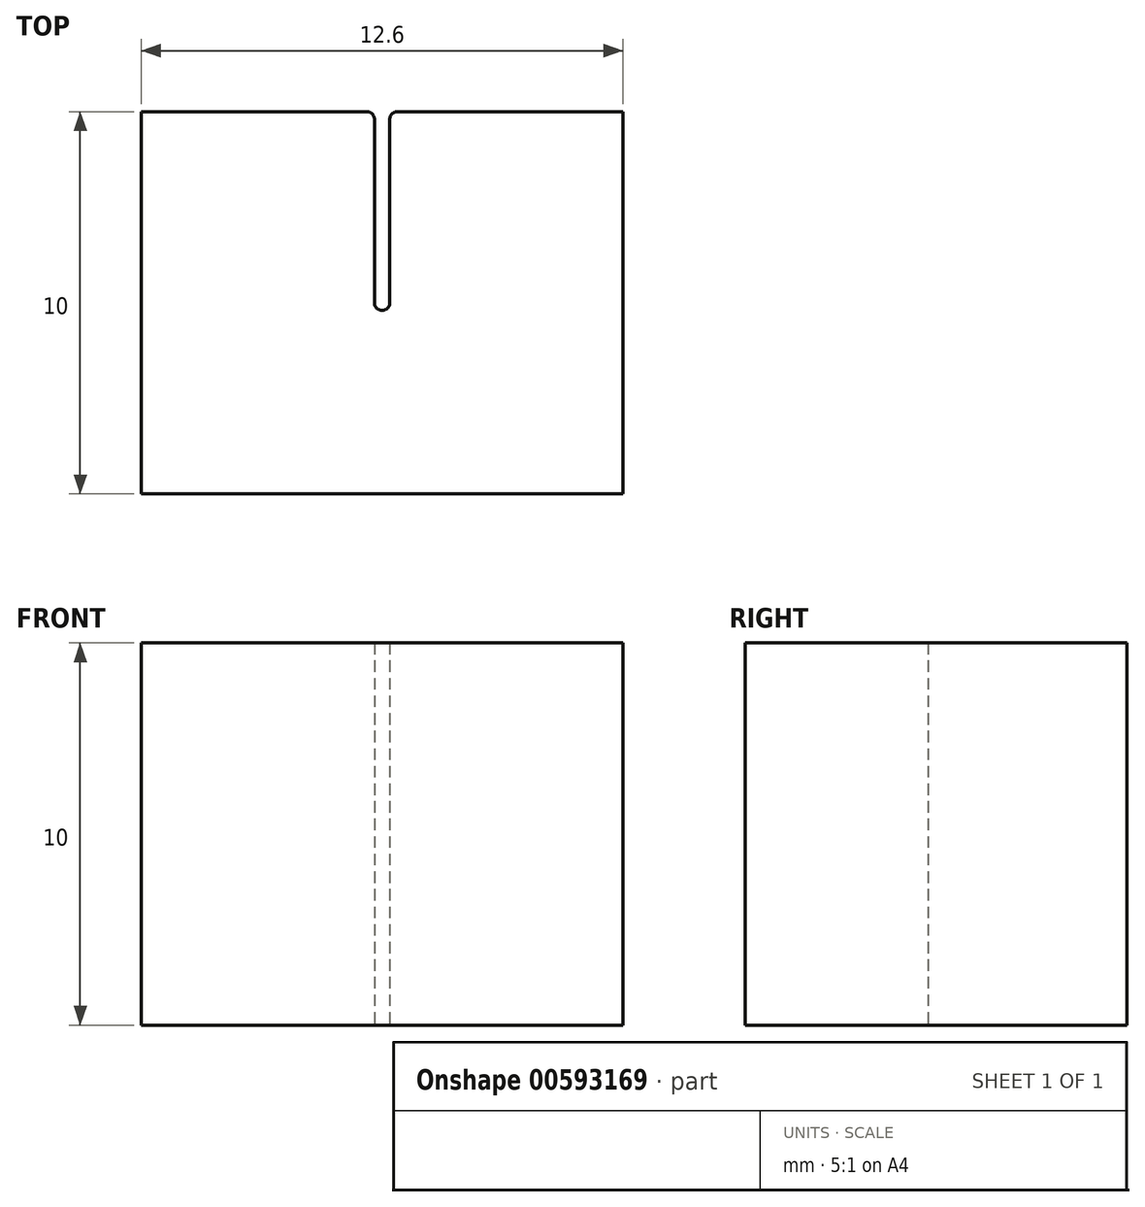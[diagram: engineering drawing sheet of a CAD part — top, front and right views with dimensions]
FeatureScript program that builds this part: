
annotation { "Feature Type Name" : "Feature", "Feature Type Description" : "" }
export const myFeature = defineFeature(function(context is Context, id is Id, definition is map)
    precondition{}
    {
        {
            var Q0;
            Q0=qCreatedBy(makeId("Top.planeOp"),FACE);
            var sketch = newSketch(context, id + "F0", { "sketchPlane" : qUnion([Q0])});
            skLineSegment(sketch, "E0.bottom", {"start": v(-6.3, 5) * mm, "end": v(-0.4, 5) * mm});
            skLineSegment(sketch, "E0.top", {"start": v(-6.3, -5) * mm, "end": v(6.3, -5) * mm});
            skLineSegment(sketch, "E0.left", {"start": v(-6.3, 5) * mm, "end": v(-6.3, -5) * mm});
            skLineSegment(sketch, "E0.right", {"start": v(6.3, 5) * mm, "end": v(6.3, -5) * mm});
            skLineSegment(sketch, "E1.top", {"start": v(0, -0.2) * mm, "end": v(0, -0.2) * mm});
            skLineSegment(sketch, "E1.left", {"start": v(-0.2, 4.8) * mm, "end": v(-0.2, 0) * mm});
            skLineSegment(sketch, "E1.right", {"start": v(0.2, 4.8) * mm, "end": v(0.2, 0) * mm});
            skLineSegment(sketch, "E2.trimOffspring", {"start": v(0.4, 5) * mm, "end": v(6.3, 5) * mm});
            skPoint(sketch, "E3.visualSharp", {"position": v(-0.2, -0.2) * mm});
            skArc(sketch, "E3.filletArc", {"start": v(-0.2, 0) * mm, "mid": v(-0.14, -0.14) * mm, "end": v(0, -0.2) * mm});
            skPoint(sketch, "E4.visualSharp", {"position": v(0.2, -0.2) * mm});
            skArc(sketch, "E4.filletArc", {"start": v(0, -0.2) * mm, "mid": v(0.14, -0.14) * mm, "end": v(0.2, 0) * mm});
            skPoint(sketch, "E5.visualSharp", {"position": v(-0.2, 5) * mm});
            skArc(sketch, "E5.filletArc", {"start": v(-0.2, 4.8) * mm, "mid": v(-0.26, 4.94) * mm, "end": v(-0.4, 5) * mm});
            skPoint(sketch, "E6.visualSharp", {"position": v(0.2, 5) * mm});
            skArc(sketch, "E6.filletArc", {"start": v(0.4, 5) * mm, "mid": v(0.26, 4.94) * mm, "end": v(0.2, 4.8) * mm});
            skSolve(sketch);
        }
        {
            var Q0;
            Q0 = qSketchRegion(id + "F0", true);
            extrude(context, id + "F1", {"entities" : qUnion([Q0]), "depth" : 10 * mm, "offsetDistance" : 25 * mm});
        }
    });
